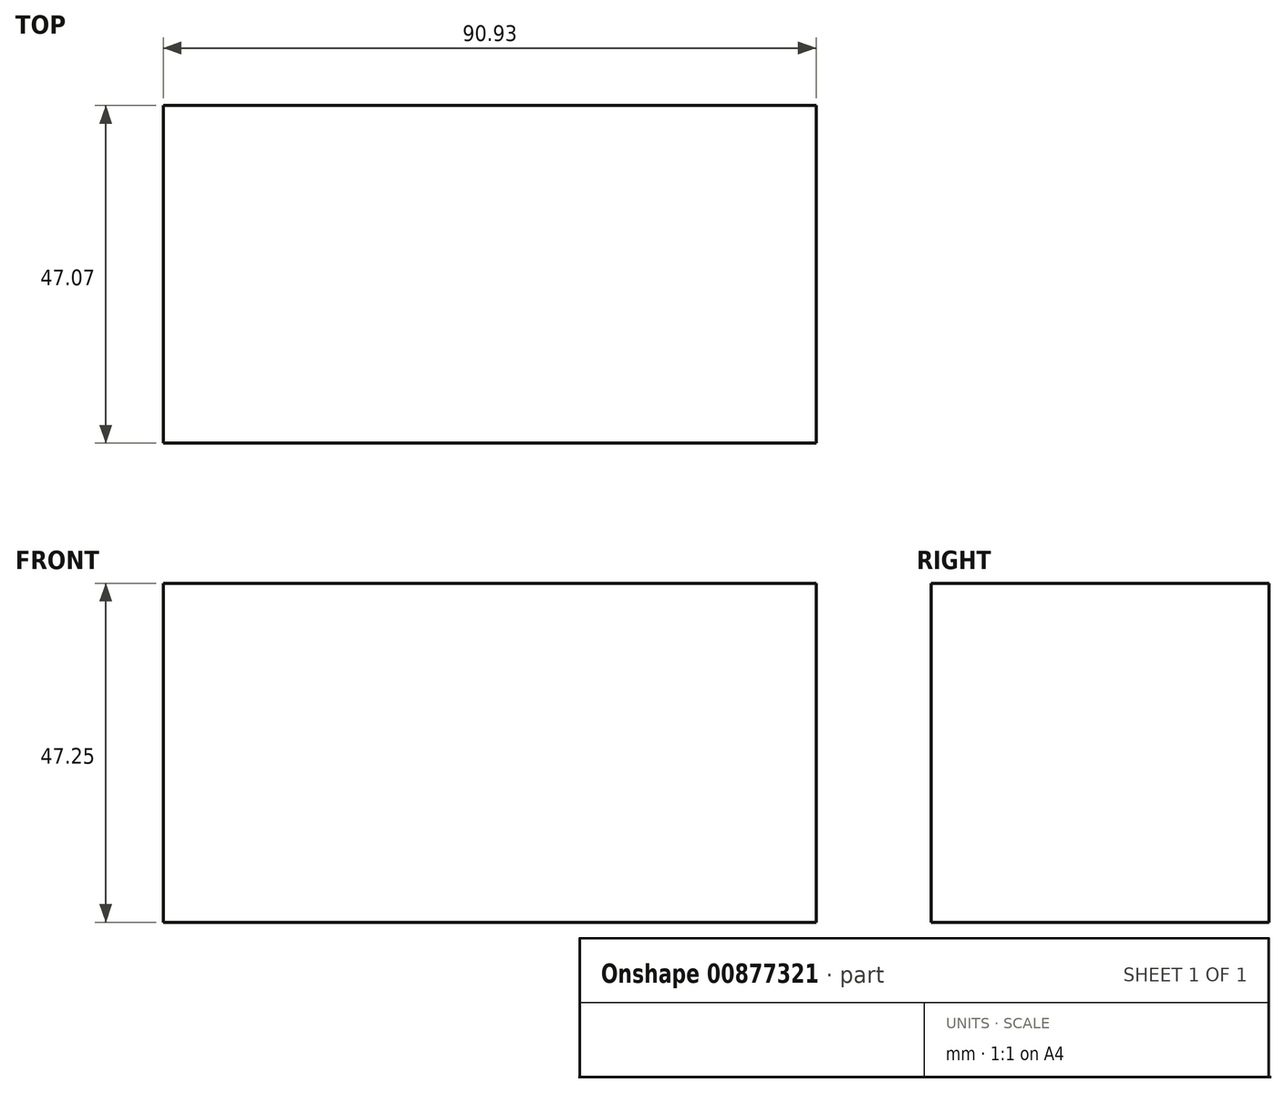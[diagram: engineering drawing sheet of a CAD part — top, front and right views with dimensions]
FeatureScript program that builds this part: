
annotation { "Feature Type Name" : "Feature", "Feature Type Description" : "" }
export const myFeature = defineFeature(function(context is Context, id is Id, definition is map)
    precondition{}
    {
        {
            var Q0;
            Q0=qCreatedBy(makeId("Right.planeOp"),FACE);
            var sketch = newSketch(context, id + "F0", { "sketchPlane" : qUnion([Q0])});
            skLineSegment(sketch, "E0.bottom", {"start": v(-19.28, 28.33) * mm, "end": v(27.79, 28.33) * mm});
            skLineSegment(sketch, "E0.top", {"start": v(-19.28, -18.92) * mm, "end": v(27.79, -18.92) * mm});
            skLineSegment(sketch, "E0.left", {"start": v(-19.28, 28.33) * mm, "end": v(-19.28, -18.92) * mm});
            skLineSegment(sketch, "E0.right", {"start": v(27.79, 28.33) * mm, "end": v(27.79, -18.92) * mm});
            skSolve(sketch);
        }
        {
            var Q0;
            Q0=makeQuery(id+"F0.imprint","IMPRINT",FACE,{"disambiguationData":[TD([[makeQuery(id+"F0.imprint","IMPRINT",EDGE,{"derivedFrom":sQuery(id+"F0.wireOp",EDGE,"E0.bottom")}),-1.0]])]});
            extrude(context, id + "F1", {"entities" : qUnion([Q0]), "depth" : 90.93 * mm, "offsetDistance" : 25.4 * mm});
        }
    });
